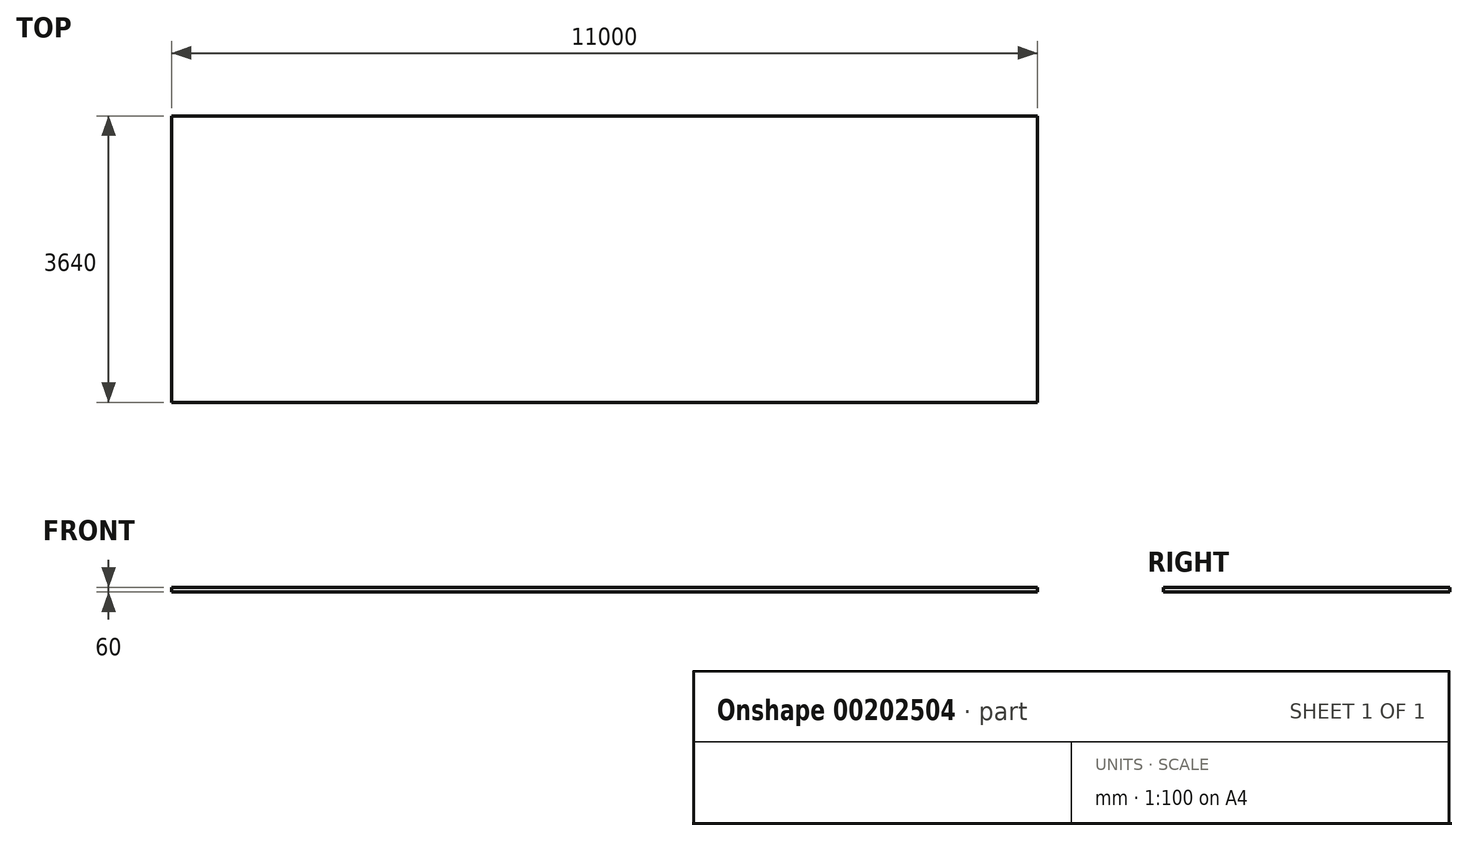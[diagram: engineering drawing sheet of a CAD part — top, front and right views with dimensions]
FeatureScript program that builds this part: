
annotation { "Feature Type Name" : "Feature", "Feature Type Description" : "" }
export const myFeature = defineFeature(function(context is Context, id is Id, definition is map)
    precondition{}
    {
        {
            var Q0;
            Q0=qCreatedBy(makeId("Top.planeOp"),FACE);
            var sketch = newSketch(context, id + "F0", { "sketchPlane" : qUnion([Q0])});
            skLineSegment(sketch, "E0.bottom", {"start": v(-5663.8, 1570.83) * mm, "end": v(5336.2, 1570.83) * mm});
            skLineSegment(sketch, "E0.top", {"start": v(-5663.8, -2069.17) * mm, "end": v(5336.2, -2069.17) * mm});
            skLineSegment(sketch, "E0.left", {"start": v(-5663.8, 1570.83) * mm, "end": v(-5663.8, -2069.17) * mm});
            skLineSegment(sketch, "E0.right", {"start": v(5336.2, 1570.83) * mm, "end": v(5336.2, -2069.17) * mm});
            skSolve(sketch);
        }
        {
            var Q0;
            Q0=makeQuery(id+"F0.imprint","IMPRINT",FACE,{"disambiguationData":[TD([[makeQuery(id+"F0.imprint","IMPRINT",EDGE,{"derivedFrom":sQuery(id+"F0.wireOp",EDGE,"E0.bottom")}),-1.0]])]});
            extrude(context, id + "F1", {"entities" : qUnion([Q0]), "depth" : 60 * mm});
        }
    });
